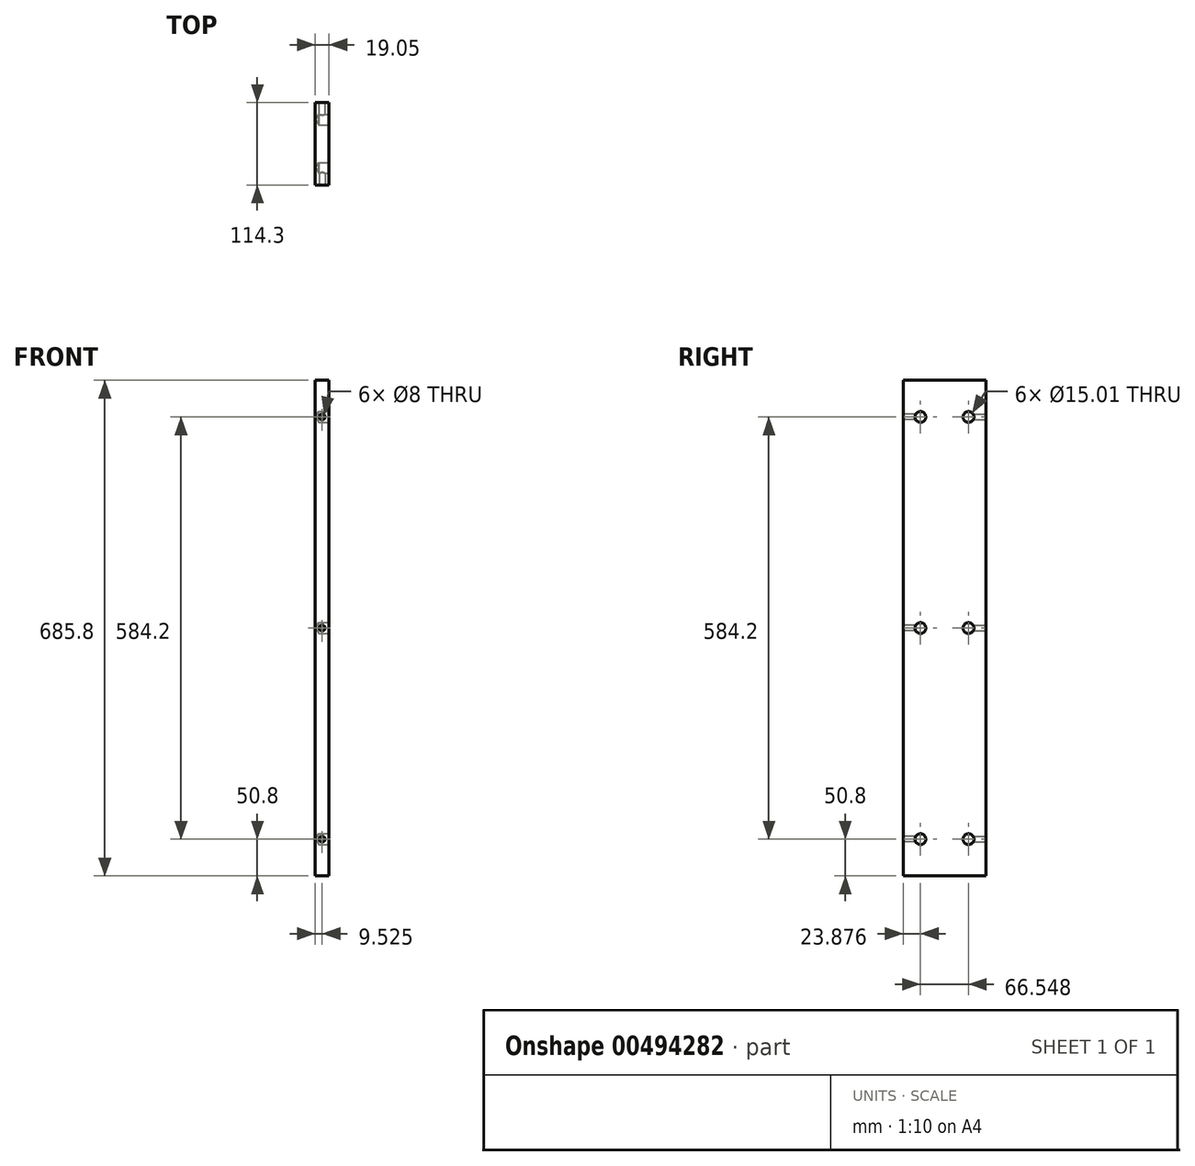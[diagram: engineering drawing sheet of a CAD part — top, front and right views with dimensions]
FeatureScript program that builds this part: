
annotation { "Feature Type Name" : "Feature", "Feature Type Description" : "" }
export const myFeature = defineFeature(function(context is Context, id is Id, definition is map)
    precondition{}
    {
        {
            var Q0;
            Q0=qCreatedBy(makeId("Right.planeOp"),FACE);
            var sketch = newSketch(context, id + "F0", { "sketchPlane" : qUnion([Q0])});
            skLineSegment(sketch, "E0.bottom", {"start": v(57.15, 342.9) * mm, "end": v(-57.15, 342.9) * mm});
            skLineSegment(sketch, "E0.top", {"start": v(57.15, -342.9) * mm, "end": v(-57.15, -342.9) * mm});
            skLineSegment(sketch, "E0.left", {"start": v(57.15, 342.9) * mm, "end": v(57.15, -342.9) * mm});
            skLineSegment(sketch, "E0.right", {"start": v(-57.15, 342.9) * mm, "end": v(-57.15, -342.9) * mm});
            skPoint(sketch, "E0.middle", {"position": v(0, 0) * mm});
            skSolve(sketch);
        }
        {
            var Q0;
            Q0 = qSketchRegion(id + "F0", true);
            extrude(context, id + "F1", {"entities" : qUnion([Q0]), "depth" : 19.05 * mm});
        }
        {
            var Q0;
            Q0=makeQuery(id+"F1.opExtrude","CAP_FACE",FACE,{"disambiguationData":[OSD([sQuery(id+"F0.wireOp",EDGE,"E0.bottom"),sQuery(id+"F0.wireOp",EDGE,"E0.top"),sQuery(id+"F0.wireOp",EDGE,"E0.left"),sQuery(id+"F0.wireOp",EDGE,"E0.right")])],"isStart":false});
            var sketch = newSketch(context, id + "F2", { "sketchPlane" : qUnion([Q0])});
            skPoint(sketch, "E1", {"position": v(-33.27, 292.1) * mm});
            skPoint(sketch, "E2", {"position": v(33.27, 292.1) * mm});
            skPoint(sketch, "E3", {"position": v(-33.27, -292.1) * mm});
            skPoint(sketch, "E4", {"position": v(33.27, -292.1) * mm});
            skPoint(sketch, "E5", {"position": v(33.27, 0) * mm});
            skPoint(sketch, "E6", {"position": v(-33.27, 0) * mm});
            skSolve(sketch);
        }
        {
            var Q0;
            Q0=sQuery(id+"F2.wireOp",VERTEX,"E1");
            var Q1;
            Q1=sQuery(id+"F2.wireOp",VERTEX,"E2");
            var Q2;
            Q2=sQuery(id+"F2.wireOp",VERTEX,"E6");
            var Q3;
            Q3=sQuery(id+"F2.wireOp",VERTEX,"E5");
            var Q4;
            Q4=sQuery(id+"F2.wireOp",VERTEX,"E4");
            var Q5;
            Q5=sQuery(id+"F2.wireOp",VERTEX,"E3");
            var Q6;
            Q6=makeQuery(id+"F1.opExtrude","SWEPT_BODY",BODY,{"disambiguationData":[OSD([sQuery(id+"F0.wireOp",EDGE,"E0.bottom"),sQuery(id+"F0.wireOp",EDGE,"E0.top"),sQuery(id+"F0.wireOp",EDGE,"E0.left"),sQuery(id+"F0.wireOp",EDGE,"E0.right")])]});
            hole(context, id + "F3", {"style" : HoleStyle.SIMPLE, "endStyle" : HoleEndStyle.BLIND, "holeDiameter" : 15 * mm, "holeDepth" : 14.22 * mm, "isTappedThrough" : true, "tappedDepth" : 12.7 * mm, "tapClearance" : 3, "startFromSketch" : true, "locations" : qUnion([Q0, Q1, Q2, Q3, Q4, Q5]), "scope" : qUnion([Q6])});
        }
        {
            var Q0;
            Q0=makeQuery(id+"F1.opExtrude","SWEPT_FACE",FACE,{"disambiguationData":[OSD([sQuery(id+"F0.wireOp",EDGE,"E0.left")])]});
            var sketch = newSketch(context, id + "F4", { "sketchPlane" : qUnion([Q0])});
            skPoint(sketch, "E7.endSnap0", {"position": v(-9.53, 342.9) * mm});
            skPoint(sketch, "E8", {"position": v(-9.53, -292.1) * mm});
            skPoint(sketch, "E9", {"position": v(-9.53, 0) * mm});
            skPoint(sketch, "E10", {"position": v(-9.53, 292.1) * mm});
            skSolve(sketch);
        }
        {
            var Q0;
            Q0=sQuery(id+"F4.wireOp",VERTEX,"E8");
            var Q1;
            Q1=sQuery(id+"F4.wireOp",VERTEX,"E10");
            var Q2;
            Q2=sQuery(id+"F4.wireOp",VERTEX,"E9");
            var Q3;
            Q3=makeQuery(id+"F1.opExtrude","SWEPT_BODY",BODY,{"disambiguationData":[OSD([sQuery(id+"F0.wireOp",EDGE,"E0.bottom"),sQuery(id+"F0.wireOp",EDGE,"E0.top"),sQuery(id+"F0.wireOp",EDGE,"E0.left"),sQuery(id+"F0.wireOp",EDGE,"E0.right")])]});
            hole(context, id + "F5", {"style" : HoleStyle.SIMPLE, "endStyle" : HoleEndStyle.BLIND, "holeDiameter" : 8 * mm, "holeDepth" : 25.4 * mm, "isTappedThrough" : true, "tappedDepth" : 12.7 * mm, "tapClearance" : 3, "startFromSketch" : true, "locations" : qUnion([Q0, Q1, Q2]), "scope" : qUnion([Q3])});
        }
        {
            var Q0;
            Q0=makeQuery(id+"F1.opExtrude","SWEPT_FACE",FACE,{"disambiguationData":[OSD([sQuery(id+"F0.wireOp",EDGE,"E0.right")])]});
            var sketch = newSketch(context, id + "F6", { "sketchPlane" : qUnion([Q0])});
            skPoint(sketch, "E11", {"position": v(9.53, 292.1) * mm});
            skPoint(sketch, "E12", {"position": v(9.53, -292.1) * mm});
            skPoint(sketch, "E13", {"position": v(9.53, 0) * mm});
            skSolve(sketch);
        }
        {
            var Q0;
            Q0=sQuery(id+"F6.wireOp",VERTEX,"E11");
            var Q1;
            Q1=sQuery(id+"F6.wireOp",VERTEX,"E13");
            var Q2;
            Q2=sQuery(id+"F6.wireOp",VERTEX,"E12");
            var Q3;
            Q3=makeQuery(id+"F1.opExtrude","SWEPT_BODY",BODY,{"disambiguationData":[OSD([sQuery(id+"F0.wireOp",EDGE,"E0.bottom"),sQuery(id+"F0.wireOp",EDGE,"E0.top"),sQuery(id+"F0.wireOp",EDGE,"E0.left"),sQuery(id+"F0.wireOp",EDGE,"E0.right")])]});
            hole(context, id + "F7", {"style" : HoleStyle.SIMPLE, "endStyle" : HoleEndStyle.BLIND, "holeDiameter" : 8 * mm, "holeDepth" : 25.4 * mm, "isTappedThrough" : true, "tappedDepth" : 12.7 * mm, "tapClearance" : 3, "startFromSketch" : true, "locations" : qUnion([Q0, Q1, Q2]), "scope" : qUnion([Q3])});
        }
    });
